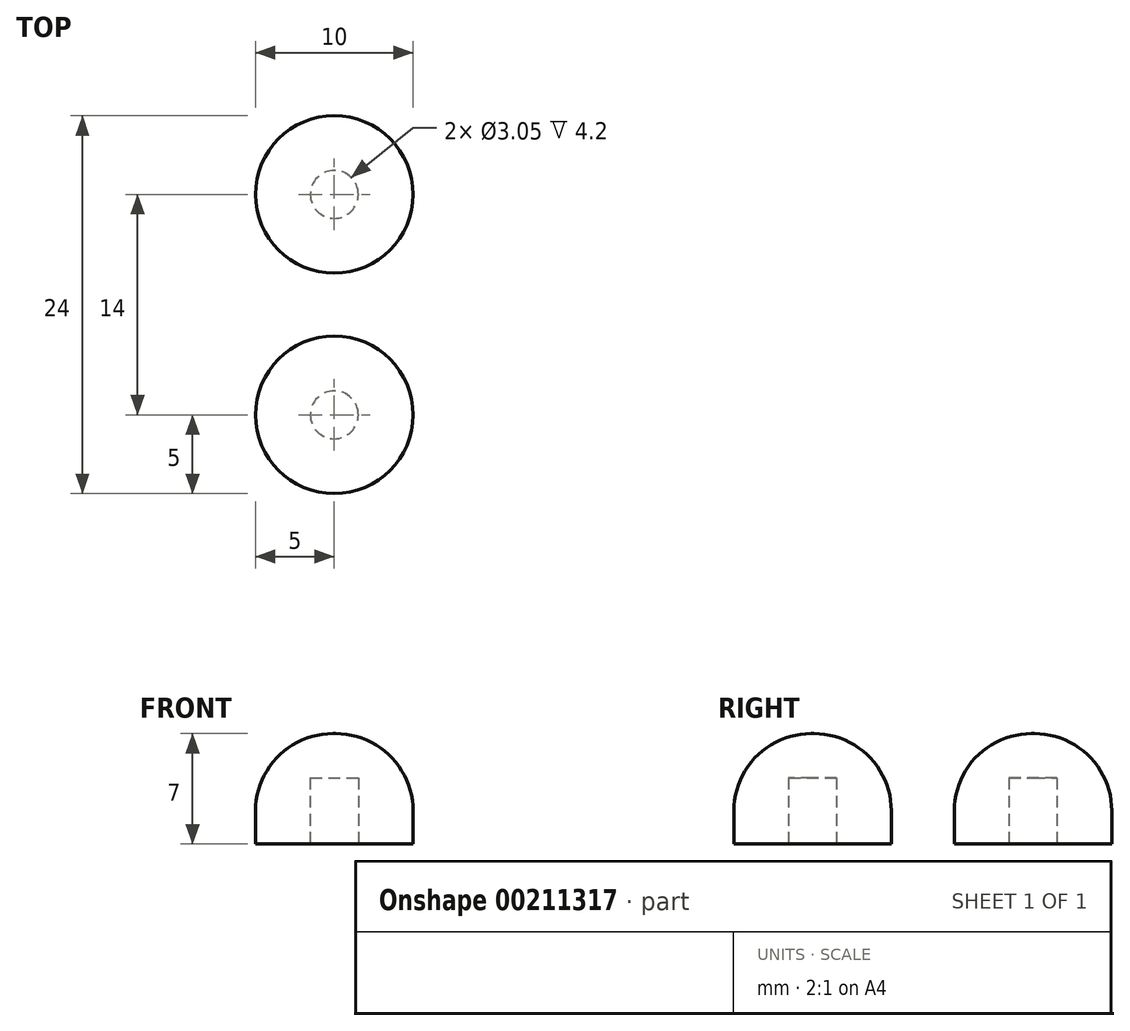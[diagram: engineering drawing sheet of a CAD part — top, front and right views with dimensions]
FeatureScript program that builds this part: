
annotation { "Feature Type Name" : "Feature", "Feature Type Description" : "" }
export const myFeature = defineFeature(function(context is Context, id is Id, definition is map)
    precondition{}
    {
        {
            var Q0;
            Q0=qCreatedBy(makeId("Top.planeOp"),FACE);
            var sketch = newSketch(context, id + "F0", { "sketchPlane" : qUnion([Q0])});
            skCircle(sketch, "E0", {"center": v(0, 0) * mm, "radius": 5 * mm});
            skSolve(sketch);
        }
        {
            var Q0;
            Q0=makeQuery(id+"F0.imprint","IMPRINT",FACE,{"disambiguationData":[TD([[makeQuery(id+"F0.imprint","IMPRINT",EDGE,{"derivedFrom":sQuery(id+"F0.wireOp",EDGE,"E0")}),1.0]])]});
            extrude(context, id + "F1", {"entities" : qUnion([Q0]), "depth" : 7 * mm});
        }
        {
            var Q0;
            Q0=makeQuery(id+"F1.opExtrude","CAP_EDGE",EDGE,{"disambiguationData":[OSD([sQuery(id+"F0.wireOp",EDGE,"E0")])],"isStart":false});
            fillet(context, id + "F2", {"entities" : qUnion([Q0]), "radius" : 4.9 * mm, "tangentPropagation" : true, "allowEdgeOverflow" : false});
        }
        {
            var Q0;
            Q0=makeQuery(id+"F1.opExtrude","CAP_FACE",FACE,{"disambiguationData":[OSD([sQuery(id+"F0.wireOp",EDGE,"E0")])],"isStart":true});
            var sketch = newSketch(context, id + "F3", { "sketchPlane" : qUnion([Q0])});
            skCircle(sketch, "E1", {"center": v(0, 0) * mm, "radius": 1.52 * mm});
            skSolve(sketch);
        }
        {
            var Q0;
            Q0=makeQuery(id+"F3.imprint","IMPRINT",FACE,{"disambiguationData":[TD([[makeQuery(id+"F3.imprint","IMPRINT",EDGE,{"derivedFrom":sQuery(id+"F3.wireOp",EDGE,"E1")}),1.0]])]});
            extrude(context, id + "F4", {"entities" : qUnion([Q0]), "operationType" : NewBodyOperationType.REMOVE, "oppositeDirection" : true, "depth" : 4.2 * mm});
        }
        {
            var Q0;
            Q0=qCreatedBy(makeId("Front.planeOp"),FACE);
            cPlane(context, id + "F5", {"entities" : qUnion([Q0]), "cplaneType" : CPlaneType.OFFSET, "offset" : 7 * mm, "width" : 152.4 * mm, "height" : 152.4 * mm});
        }
        {
            var Q0;
            Q0=makeQuery(id+"F1.opExtrude","SWEPT_BODY",BODY,{"disambiguationData":[OSD([sQuery(id+"F0.wireOp",EDGE,"E0")])]});
            var Q1;
            Q1=qCreatedBy(id+"F5.planeOp",FACE);
            mirror(context, id + "F6", {"entities" : qUnion([Q0]), "mirrorPlane" : qUnion([Q1])});
        }
    });
